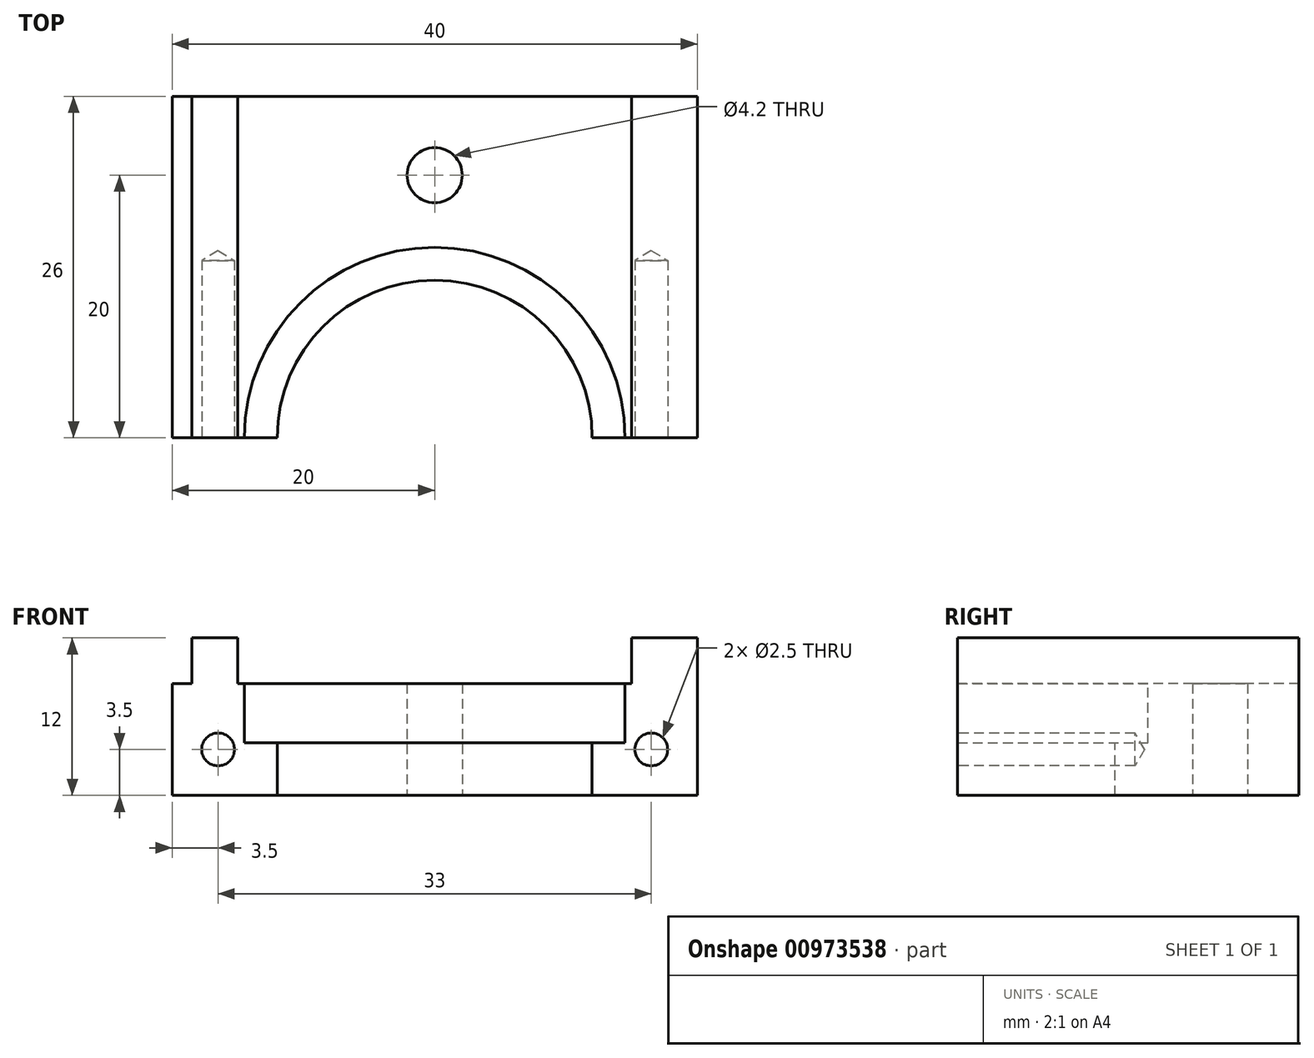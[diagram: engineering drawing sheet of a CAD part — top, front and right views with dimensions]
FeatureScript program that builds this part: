
annotation { "Feature Type Name" : "Feature", "Feature Type Description" : "" }
export const myFeature = defineFeature(function(context is Context, id is Id, definition is map)
    precondition{}
    {
        {
            var Q0;
            Q0=qCreatedBy(makeId("Front.planeOp"),FACE);
            var sketch = newSketch(context, id + "F0", { "sketchPlane" : qUnion([Q0])});
            skLineSegment(sketch, "E0.bottom", {"start": v(-20, 12) * mm, "end": v(20, 12) * mm});
            skLineSegment(sketch, "E0.top", {"start": v(-20, 0) * mm, "end": v(20, 0) * mm});
            skLineSegment(sketch, "E0.left", {"start": v(-20, 12) * mm, "end": v(-20, 0) * mm});
            skLineSegment(sketch, "E0.right", {"start": v(20, 12) * mm, "end": v(20, 0) * mm});
            skSolve(sketch);
        }
        {
            var Q0;
            Q0=makeQuery(id+"F0.imprint","IMPRINT",FACE,{"disambiguationData":[TD([[makeQuery(id+"F0.imprint","IMPRINT",EDGE,{"derivedFrom":sQuery(id+"F0.wireOp",EDGE,"E0.bottom")}),-1.0]])]});
            extrude(context, id + "F1", {"entities" : qUnion([Q0]), "oppositeDirection" : true, "depth" : 26 * mm, "offsetDistance" : 25 * mm});
        }
        {
            var Q0;
            Q0=makeQuery(id+"F1.opExtrude","CAP_FACE",FACE,{"disambiguationData":[OSD([sQuery(id+"F0.wireOp",EDGE,"E0.bottom"),sQuery(id+"F0.wireOp",EDGE,"E0.top"),sQuery(id+"F0.wireOp",EDGE,"E0.left"),sQuery(id+"F0.wireOp",EDGE,"E0.right")])],"isStart":true});
            var sketch = newSketch(context, id + "F2", { "sketchPlane" : qUnion([Q0])});
            skLineSegment(sketch, "E1.bottom", {"start": v(-15, 12) * mm, "end": v(15, 12) * mm});
            skLineSegment(sketch, "E1.top", {"start": v(-15, 8.5) * mm, "end": v(15, 8.5) * mm});
            skLineSegment(sketch, "E1.left", {"start": v(-15, 12) * mm, "end": v(-15, 8.5) * mm});
            skLineSegment(sketch, "E1.right", {"start": v(15, 12) * mm, "end": v(15, 8.5) * mm});
            skSolve(sketch);
        }
        {
            var Q0;
            Q0=makeQuery(id+"F2.imprint","IMPRINT",FACE,{"disambiguationData":[TD([[makeQuery(id+"F2.imprint","IMPRINT",EDGE,{"derivedFrom":sQuery(id+"F2.wireOp",EDGE,"E1.bottom")}),-1.0]])]});
            extrude(context, id + "F3", {"entities" : qUnion([Q0]), "operationType" : NewBodyOperationType.REMOVE, "endBound" : BoundingType.UP_TO_NEXT, "oppositeDirection" : true, "depth" : 25 * mm, "offsetDistance" : 25 * mm});
        }
        {
            var Q0;
            Q0=makeQuery(id+"F1.opExtrude","CAP_FACE",FACE,{"disambiguationData":[OSD([sQuery(id+"F0.wireOp",EDGE,"E0.bottom"),sQuery(id+"F0.wireOp",EDGE,"E0.top"),sQuery(id+"F0.wireOp",EDGE,"E0.left"),sQuery(id+"F0.wireOp",EDGE,"E0.right")])],"isStart":true});
            var sketch = newSketch(context, id + "F4", { "sketchPlane" : qUnion([Q0])});
            skLineSegment(sketch, "E2.bottom", {"start": v(-20, 12) * mm, "end": v(-18.5, 12) * mm});
            skLineSegment(sketch, "E2.top", {"start": v(-20, 8.5) * mm, "end": v(-18.5, 8.5) * mm});
            skLineSegment(sketch, "E2.left", {"start": v(-20, 12) * mm, "end": v(-20, 8.5) * mm});
            skLineSegment(sketch, "E2.right", {"start": v(-18.5, 12) * mm, "end": v(-18.5, 8.5) * mm});
            skSolve(sketch);
        }
        {
            var Q0;
            Q0=makeQuery(id+"F4.imprint","IMPRINT",FACE,{"disambiguationData":[TD([[makeQuery(id+"F4.imprint","IMPRINT",EDGE,{"derivedFrom":sQuery(id+"F4.wireOp",EDGE,"E2.bottom")}),-1.0]])]});
            extrude(context, id + "F5", {"entities" : qUnion([Q0]), "operationType" : NewBodyOperationType.REMOVE, "endBound" : BoundingType.UP_TO_NEXT, "oppositeDirection" : true, "depth" : 25 * mm, "offsetDistance" : 25 * mm});
        }
        {
            var Q0;
            {var subQ1=sQuery(id+"F0.wireOp",EDGE,"E0.left");var subQ3=sQuery(id+"F0.wireOp",EDGE,"E0.bottom");Q0=makeQuery(id+"F3.boolean.opBoolean","SPLIT",FACE,{"disambiguationData":[TD([makeQuery(id+"F1.opExtrude","SWEPT_FACE",FACE,{"disambiguationData":[OSD([subQ1])]})])],"derivedFrom":makeQuery(id+"F1.opExtrude","SWEPT_FACE",FACE,{"disambiguationData":[OSD([subQ3])]})});}
            var sketch = newSketch(context, id + "F6", { "sketchPlane" : qUnion([Q0])});
            skArc(sketch, "E3", {"start": v(12, 0) * mm, "mid": v(0, 12) * mm, "end": v(-12, 0) * mm});
            skLineSegment(sketch, "E4", {"start": v(-12, 0) * mm, "end": v(12, 0) * mm});
            skSolve(sketch);
        }
        {
            var Q0;
            {var subQ0=sQuery(id+"F6.wireOp",EDGE,"E4");var subQ1=sQuery(id+"F6.wireOp",EDGE,"E3");var subQ2=makeQuery(id+"F6.imprint","INTERSECT",VERTEX,{"derivedFrom":[subQ1,subQ0]});Q0=makeQuery(id+"F6.imprint","IMPRINT",FACE,{"disambiguationData":[TD([[makeQuery(id+"F6.imprint","IMPRINT",EDGE,{"disambiguationData":[TD([[subQ2,-1.0]])],"derivedFrom":subQ1}),1.0]])]});}
            var Q1;
            Q1=makeQuery(id+"F1.opExtrude","SWEPT_FACE",FACE,{"disambiguationData":[OSD([sQuery(id+"F0.wireOp",EDGE,"E0.top")])]});
            extrude(context, id + "F7", {"entities" : qUnion([Q0]), "operationType" : NewBodyOperationType.REMOVE, "endBound" : BoundingType.UP_TO_SURFACE, "oppositeDirection" : true, "depth" : 25 * mm, "endBoundEntityFace" : qUnion([Q1]), "offsetDistance" : 25 * mm});
        }
        {
            var Q0;
            {var subQ1=sQuery(id+"F0.wireOp",EDGE,"E0.left");var subQ3=sQuery(id+"F0.wireOp",EDGE,"E0.bottom");Q0=makeQuery(id+"F3.boolean.opBoolean","SPLIT",FACE,{"disambiguationData":[TD([makeQuery(id+"F1.opExtrude","SWEPT_FACE",FACE,{"disambiguationData":[OSD([subQ1])]})])],"derivedFrom":makeQuery(id+"F1.opExtrude","SWEPT_FACE",FACE,{"disambiguationData":[OSD([subQ3])]})});}
            var sketch = newSketch(context, id + "F8", { "sketchPlane" : qUnion([Q0])});
            skArc(sketch, "E5", {"start": v(14.5, 0) * mm, "mid": v(0, 14.5) * mm, "end": v(-14.5, 0) * mm});
            skLineSegment(sketch, "E6", {"start": v(-14.5, 0) * mm, "end": v(14.5, 0) * mm});
            skSolve(sketch);
        }
        {
            var Q0;
            {var subQ6=sQuery(id+"F2.wireOp",EDGE,"E1.left");var subQ7=makeQuery(id+"F3.opExtrude","SWEPT_FACE",FACE,{"disambiguationData":[OSD([subQ6])]});var subQ11=sQuery(id+"F6.wireOp",EDGE,"E3");var subQ12=makeQuery(id+"F7.boolean.opBoolean","COPY",EDGE,{"disambiguationData":[TD([makeQuery(id+"F3.boolean.opBoolean","COPY",FACE,{"derivedFrom":subQ7})])],"derivedFrom":makeQuery(id+"F7.opExtrude","CAP_EDGE",EDGE,{"disambiguationData":[OSD([subQ11])],"isStart":true})});Q0=makeQuery(id+"F8.imprint","IMPRINT",FACE,{"disambiguationData":[TD([[makeQuery(id+"F8.imprint","IMPRINT",EDGE,{"derivedFrom":subQ12}),-1.0]])]});}
            var Q1;
            {var subQ0=sQuery(id+"F8.wireOp",EDGE,"E6");var subQ1=sQuery(id+"F8.wireOp",EDGE,"E5");var subQ2=makeQuery(id+"F8.imprint","INTERSECT",VERTEX,{"derivedFrom":[subQ1,subQ0]});Q1=makeQuery(id+"F8.imprint","IMPRINT",FACE,{"disambiguationData":[TD([[makeQuery(id+"F8.imprint","IMPRINT",EDGE,{"disambiguationData":[TD([[subQ2,-1.0]])],"derivedFrom":subQ1}),1.0]])]});}
            extrude(context, id + "F9", {"entities" : qUnion([Q0, Q1]), "operationType" : NewBodyOperationType.REMOVE, "oppositeDirection" : true, "depth" : 8 * mm, "offsetDistance" : 25 * mm});
        }
        {
            var Q0;
            {var subQ0=sQuery(id+"F0.wireOp",EDGE,"E0.top");var subQ1=sQuery(id+"F0.wireOp",EDGE,"E0.left");var subQ2=sQuery(id+"F0.wireOp",EDGE,"E0.bottom");Q0=makeQuery(id+"F7.boolean.opBoolean","SPLIT",FACE,{"disambiguationData":[TD([makeQuery(id+"F1.opExtrude","SWEPT_FACE",FACE,{"disambiguationData":[OSD([subQ1])]})])],"derivedFrom":makeQuery(id+"F1.opExtrude","CAP_FACE",FACE,{"disambiguationData":[OSD([subQ2,subQ0,subQ1,sQuery(id+"F0.wireOp",EDGE,"E0.right")])],"isStart":true})});}
            var sketch = newSketch(context, id + "F10", { "sketchPlane" : qUnion([Q0])});
            skPoint(sketch, "E7", {"position": v(-16.5, 3.5) * mm});
            skPoint(sketch, "E8", {"position": v(16.5, 3.5) * mm});
            skSolve(sketch);
        }
        {
            var Q0;
            Q0=sQuery(id+"F10.wireOp",VERTEX,"E7");
            var Q1;
            Q1=sQuery(id+"F10.wireOp",VERTEX,"E8");
            var Q2;
            Q2=makeQuery(id+"F1.opExtrude","SWEPT_BODY",BODY,{"disambiguationData":[OSD([sQuery(id+"F0.wireOp",EDGE,"E0.bottom"),sQuery(id+"F0.wireOp",EDGE,"E0.top"),sQuery(id+"F0.wireOp",EDGE,"E0.left"),sQuery(id+"F0.wireOp",EDGE,"E0.right")])]});
            hole(context, id + "F11", {"style" : HoleStyle.SIMPLE, "endStyle" : HoleEndStyle.BLIND, "standardTappedOrClearance" : lookupTablePath({ "standard" : "ISO", "engagement" : "75%", "pitch" : "0.5 mm", "size" : "M3", "type" : "Tapped" }), "standardBlindInLast" : lookupTablePath({ "standard" : "ISO", "fit" : "Normal", "engagement" : "75%", "pitch" : "0.5 mm", "size" : "M3", "type" : "Clearance & tapped" }), "holeDiameter" : 2.5 * mm, "majorDiameter" : 3 * mm, "showTappedDepth" : true, "holeDepth" : 13.5 * mm, "isTappedThrough" : true, "tappedDepth" : 12 * mm, "tapClearance" : 3, "startFromSketch" : true, "locations" : qUnion([Q0, Q1]), "scope" : qUnion([Q2])});
        }
        {
            var Q0;
            Q0=makeQuery(id+"F1.opExtrude","SWEPT_FACE",FACE,{"disambiguationData":[OSD([sQuery(id+"F0.wireOp",EDGE,"E0.top")])]});
            var sketch = newSketch(context, id + "F12", { "sketchPlane" : qUnion([Q0])});
            skCircle(sketch, "E9", {"center": v(0, 0) * mm, "radius": 14 * mm, "construction": true});
            skPoint(sketch, "E10", {"position": v(0, -20) * mm});
            skSolve(sketch);
        }
        {
            var Q0;
            Q0=sQuery(id+"F12.wireOp",VERTEX,"E10");
            var Q1;
            Q1=makeQuery(id+"F1.opExtrude","SWEPT_BODY",BODY,{"disambiguationData":[OSD([sQuery(id+"F0.wireOp",EDGE,"E0.bottom"),sQuery(id+"F0.wireOp",EDGE,"E0.top"),sQuery(id+"F0.wireOp",EDGE,"E0.left"),sQuery(id+"F0.wireOp",EDGE,"E0.right")])]});
            hole(context, id + "F13", {"style" : HoleStyle.SIMPLE, "endStyle" : HoleEndStyle.THROUGH, "standardTappedOrClearance" : lookupTablePath({ "standard" : "ISO", "engagement" : "75%", "pitch" : "0.8 mm", "size" : "M5", "type" : "Tapped" }), "standardBlindInLast" : lookupTablePath({ "standard" : "ISO", "fit" : "Normal", "engagement" : "75%", "pitch" : "0.8 mm", "size" : "M5", "type" : "Clearance & tapped" }), "holeDiameter" : 4.2 * mm, "majorDiameter" : 5 * mm, "showTappedDepth" : true, "isTappedThrough" : true, "tappedDepth" : 12 * mm, "tapClearance" : 3, "startFromSketch" : true, "locations" : qUnion([Q0]), "scope" : qUnion([Q1])});
        }
    });
